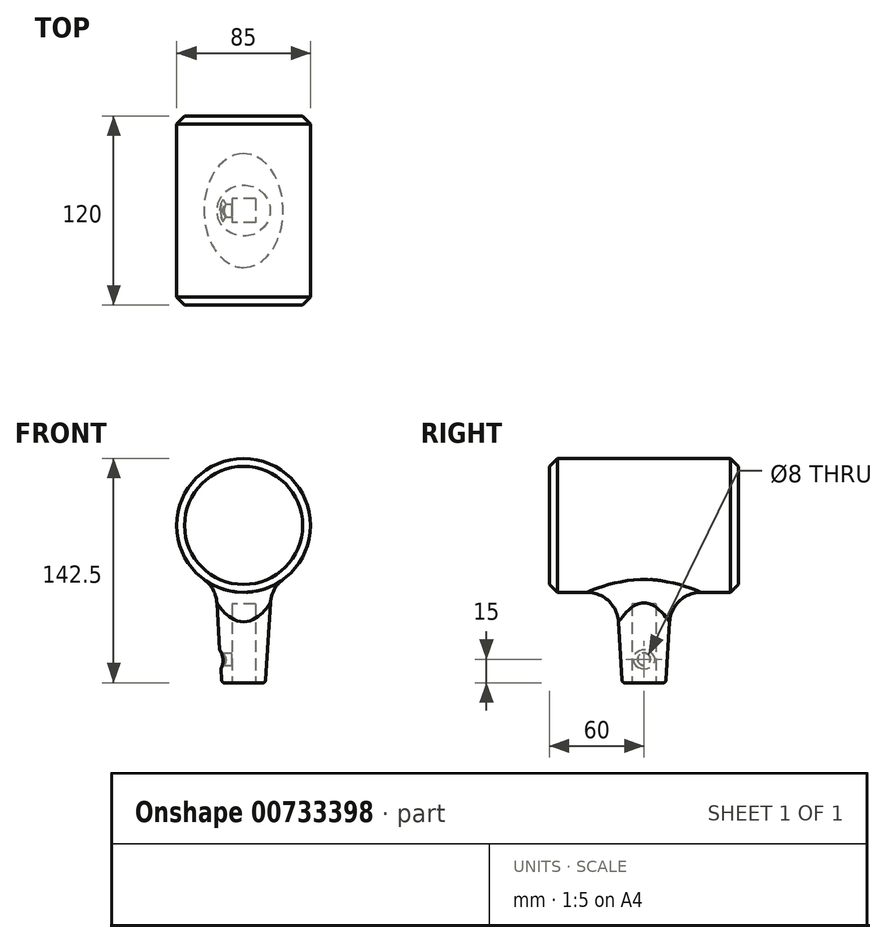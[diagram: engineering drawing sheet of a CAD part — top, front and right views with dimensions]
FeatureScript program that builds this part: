
annotation { "Feature Type Name" : "Feature", "Feature Type Description" : "" }
export const myFeature = defineFeature(function(context is Context, id is Id, definition is map)
    precondition{}
    {
        {
            var Q0;
            Q0=qCreatedBy(makeId("Front.planeOp"),FACE);
            var sketch = newSketch(context, id + "F0", { "sketchPlane" : qUnion([Q0])});
            skCircle(sketch, "E0", {"center": v(0, 0) * mm, "radius": 42.5 * mm});
            skSolve(sketch);
        }
        {
            var Q0;
            Q0=makeQuery(id+"F0.imprint","IMPRINT",FACE,{"disambiguationData":[TD([[makeQuery(id+"F0.imprint","IMPRINT",EDGE,{"derivedFrom":sQuery(id+"F0.wireOp",EDGE,"E0")}),1.0]])]});
            var Q1;
            Q1=sQuery(id+"F0.wireOp",EDGE,"E0");
            extrude(context, id + "F1", {"entities" : qUnion([Q0]), "surfaceEntities" : qUnion([Q1]), "endBound" : BoundingType.SYMMETRIC, "oppositeDirection" : true, "depth" : 120 * mm, "offsetDistance" : 25 * mm});
        }
        {
            var Q0;
            Q0=qCreatedBy(makeId("Top.planeOp"),FACE);
            var sketch = newSketch(context, id + "F2", { "sketchPlane" : qUnion([Q0])});
            skCircle(sketch, "E1", {"center": v(0, 0) * mm, "radius": 20 * mm});
            skSolve(sketch);
        }
        {
            var Q0;
            Q0 = qSketchRegion(id + "F2", true);
            extrude(context, id + "F3", {"entities" : qUnion([Q0]), "operationType" : NewBodyOperationType.ADD, "oppositeDirection" : true, "depth" : 100 * mm, "offsetDistance" : 25 * mm, "hasDraft" : true, "draftAngle" : 3.5 * degree, "draftPullDirection" : true});
        }
        {
            var Q0;
            Q0=makeQuery(id+"F3.opExtrude","CAP_FACE",FACE,{"disambiguationData":[OSD([sQuery(id+"F2.wireOp",EDGE,"E1")])],"isStart":false});
            var sketch = newSketch(context, id + "F4", { "sketchPlane" : qUnion([Q0])});
            skLineSegment(sketch, "E2.bottom", {"start": v(7.5, -7.5) * mm, "end": v(-7.5, -7.5) * mm});
            skLineSegment(sketch, "E2.top", {"start": v(7.5, 7.5) * mm, "end": v(-7.5, 7.5) * mm});
            skLineSegment(sketch, "E2.left", {"start": v(7.5, -7.5) * mm, "end": v(7.5, 7.5) * mm});
            skLineSegment(sketch, "E2.right", {"start": v(-7.5, -7.5) * mm, "end": v(-7.5, 7.5) * mm});
            skPoint(sketch, "E2.middle", {"position": v(0, 0) * mm});
            skSolve(sketch);
        }
        {
            var Q0;
            Q0 = qSketchRegion(id + "F4", true);
            extrude(context, id + "F5", {"entities" : qUnion([Q0]), "operationType" : NewBodyOperationType.REMOVE, "oppositeDirection" : true, "depth" : 50 * mm, "offsetDistance" : 25 * mm});
        }
        {
            var Q0;
            Q0=qCreatedBy(makeId("Right.planeOp"),FACE);
            var sketch = newSketch(context, id + "F6", { "sketchPlane" : qUnion([Q0])});
            skCircle(sketch, "E3", {"center": v(0, -85) * mm, "radius": 4 * mm});
            skSolve(sketch);
        }
        {
            var Q0;
            Q0 = qSketchRegion(id + "F6", true);
            extrude(context, id + "F7", {"entities" : qUnion([Q0]), "operationType" : NewBodyOperationType.REMOVE, "oppositeDirection" : true, "depth" : 50 * mm, "offsetDistance" : 25 * mm});
        }
        {
            var Q0;
            Q0=makeQuery(id+"F1.opExtrude","CAP_FACE",FACE,{"disambiguationData":[OSD([sQuery(id+"F0.wireOp",EDGE,"E0")])],"isStart":false});
            var Q1;
            Q1=makeQuery(id+"F1.opExtrude","CAP_FACE",FACE,{"disambiguationData":[OSD([sQuery(id+"F0.wireOp",EDGE,"E0")])],"isStart":true});
            chamfer(context, id + "F8", {"entities" : qUnion([Q0, Q1]), "width" : 5 * mm, "tangentPropagation" : true});
        }
        {
            var Q0;
            Q0=makeQuery(id+"F3.boolean.opBoolean","INTERSECT",EDGE,{"derivedFrom":[makeQuery(id+"F1.opExtrude","SWEPT_FACE",FACE,{"disambiguationData":[OSD([sQuery(id+"F0.wireOp",EDGE,"E0")])]}),makeQuery(id+"F3.opExtrude","SWEPT_FACE",FACE,{"disambiguationData":[OSD([sQuery(id+"F2.wireOp",EDGE,"E1")])]})]});
            fillet(context, id + "F9", {"entities" : qUnion([Q0]), "radius" : 20 * mm, "tangentPropagation" : true, "allowEdgeOverflow" : false});
        }
        {
            var Q0;
            Q0=makeQuery(id+"F3.opExtrude","CAP_EDGE",EDGE,{"disambiguationData":[OSD([sQuery(id+"F2.wireOp",EDGE,"E1")])],"isStart":false});
            fillet(context, id + "F10", {"entities" : qUnion([Q0]), "radius" : 2 * mm, "tangentPropagation" : true, "allowEdgeOverflow" : false});
        }
        {
            var Q0;
            Q0=makeQuery(id+"F7.boolean.opBoolean","INTERSECT",EDGE,{"derivedFrom":[makeQuery(id+"F3.opExtrude","SWEPT_FACE",FACE,{"disambiguationData":[OSD([sQuery(id+"F2.wireOp",EDGE,"E1")])]}),makeQuery(id+"F7.opExtrude","SWEPT_FACE",FACE,{"disambiguationData":[OSD([sQuery(id+"F6.wireOp",EDGE,"E3")])]})]});
            chamfer(context, id + "F11", {"entities" : qUnion([Q0]), "width" : 2 * mm, "tangentPropagation" : true});
        }
    });
